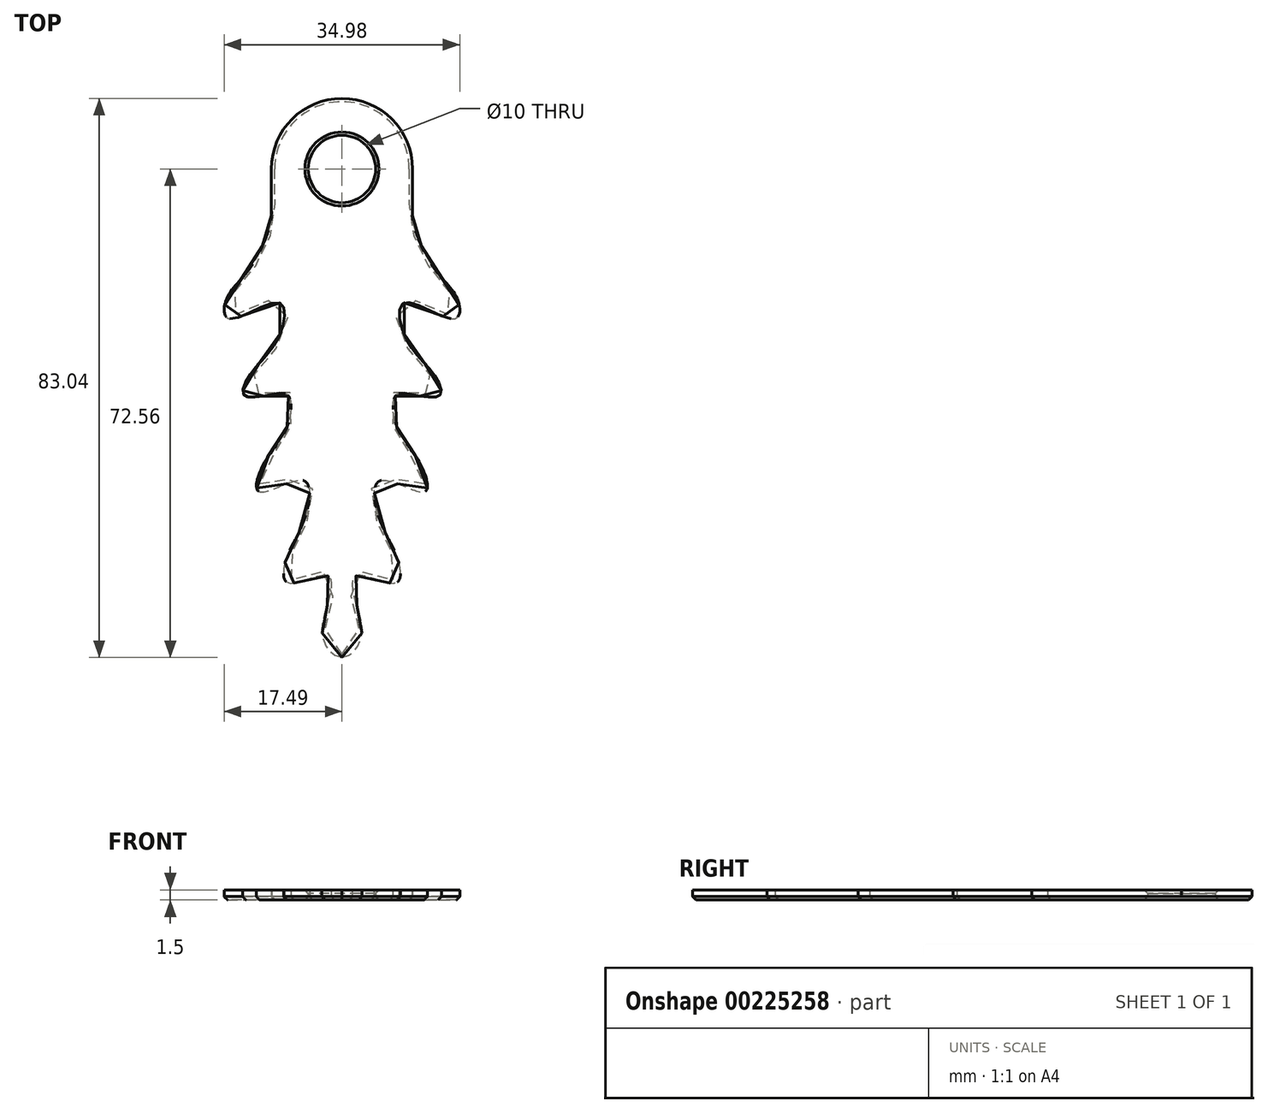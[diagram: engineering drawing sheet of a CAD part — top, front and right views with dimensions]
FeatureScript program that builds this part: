
annotation { "Feature Type Name" : "Feature", "Feature Type Description" : "" }
export const myFeature = defineFeature(function(context is Context, id is Id, definition is map)
    precondition{}
    {
        {
            var Q0;
            Q0=qCreatedBy(makeId("Top.planeOp"),FACE);
            var sketch = newSketch(context, id + "F0", { "sketchPlane" : qUnion([Q0])});
            skCircle(sketch, "E0", {"center": v(0, 0) * mm, "radius": 5 * mm});
            skFitSpline(sketch, "E1", {"points": [v(10.48, 0) * mm, v(10.75, -8.58) * mm, v(13.85, -14.98) * mm, v(17.2, -19.45) * mm, v(16.72, -22.23) * mm, v(9.26, -19.88) * mm, v(9.47, -25.1) * mm, v(13.42, -30.23) * mm, v(14.6, -33.53) * mm, v(10.65, -33.53) * mm, v(7.98, -33.64) * mm, v(8.2, -38.44) * mm, v(11.5, -43.55) * mm, v(12.25, -47.93) * mm, v(5.69, -46.29) * mm, v(5.63, -52.2) * mm, v(8.2, -57.63) * mm, v(7.98, -61.47) * mm, v(2.17, -60.35) * mm, v(2.12, -64.56) * mm, v(2.97, -68.61) * mm, v(0, -72.56) * mm], "startDerivative": vector(2.87, -268.08) * mm, "endDerivative": vector(-140.95, -28.4) * mm});
            skLineSegment(sketch, "E2", {"start": v(0, -73.94) * mm, "end": v(0, 14.45) * mm, "construction": true});
            skFitSpline(sketch, "E3.MirrorCS", {"points": [v(-10.48, 0) * mm, v(-10.75, -8.58) * mm, v(-13.85, -14.98) * mm, v(-17.2, -19.45) * mm, v(-16.72, -22.23) * mm, v(-9.26, -19.88) * mm, v(-9.47, -25.1) * mm, v(-13.42, -30.23) * mm, v(-14.6, -33.53) * mm, v(-10.65, -33.53) * mm, v(-7.98, -33.64) * mm, v(-8.2, -38.44) * mm, v(-11.5, -43.55) * mm, v(-12.25, -47.93) * mm, v(-5.69, -46.29) * mm, v(-5.63, -52.2) * mm, v(-8.2, -57.63) * mm, v(-7.98, -61.47) * mm, v(-2.17, -60.35) * mm, v(-2.12, -64.56) * mm, v(-2.97, -68.61) * mm, v(0, -72.56) * mm], "startDerivative": vector(-2.87, -268.08) * mm, "endDerivative": vector(140.95, -28.4) * mm});
            skArc(sketch, "E4", {"start": v(-10.48, 0) * mm, "mid": v(0, 10.48) * mm, "end": v(10.48, 0) * mm});
            skSolve(sketch);
        }
        {
            var Q0;
            Q0 = qSketchRegion(id + "F0", true);
            extrude(context, id + "F1", {"entities" : qUnion([Q0]), "depth" : 1.5 * mm});
        }
        {
            var Q0;
            Q0=makeQuery(id+"F1.opExtrude","CAP_EDGE",EDGE,{"disambiguationData":[OSD([sQuery(id+"F0.wireOp",EDGE,"E3.MirrorCS")])],"isStart":true});
            var Q1;
            Q1=makeQuery(id+"F1.opExtrude","CAP_EDGE",EDGE,{"disambiguationData":[OSD([sQuery(id+"F0.wireOp",EDGE,"E4")])],"isStart":true});
            chamfer(context, id + "F2", {"entities" : qUnion([Q0, Q1]), "width" : 0.5 * mm, "tangentPropagation" : true});
        }
        {
            var Q0;
            Q0=makeQuery(id+"F1.opExtrude","CAP_EDGE",EDGE,{"disambiguationData":[OSD([sQuery(id+"F0.wireOp",EDGE,"E0")])],"isStart":false});
            var Q1;
            Q1=makeQuery(id+"F1.opExtrude","CAP_EDGE",EDGE,{"disambiguationData":[OSD([sQuery(id+"F0.wireOp",EDGE,"E0")])],"isStart":true});
            chamfer(context, id + "F3", {"entities" : qUnion([Q0, Q1]), "width" : 0.5 * mm, "tangentPropagation" : true});
        }
    });
